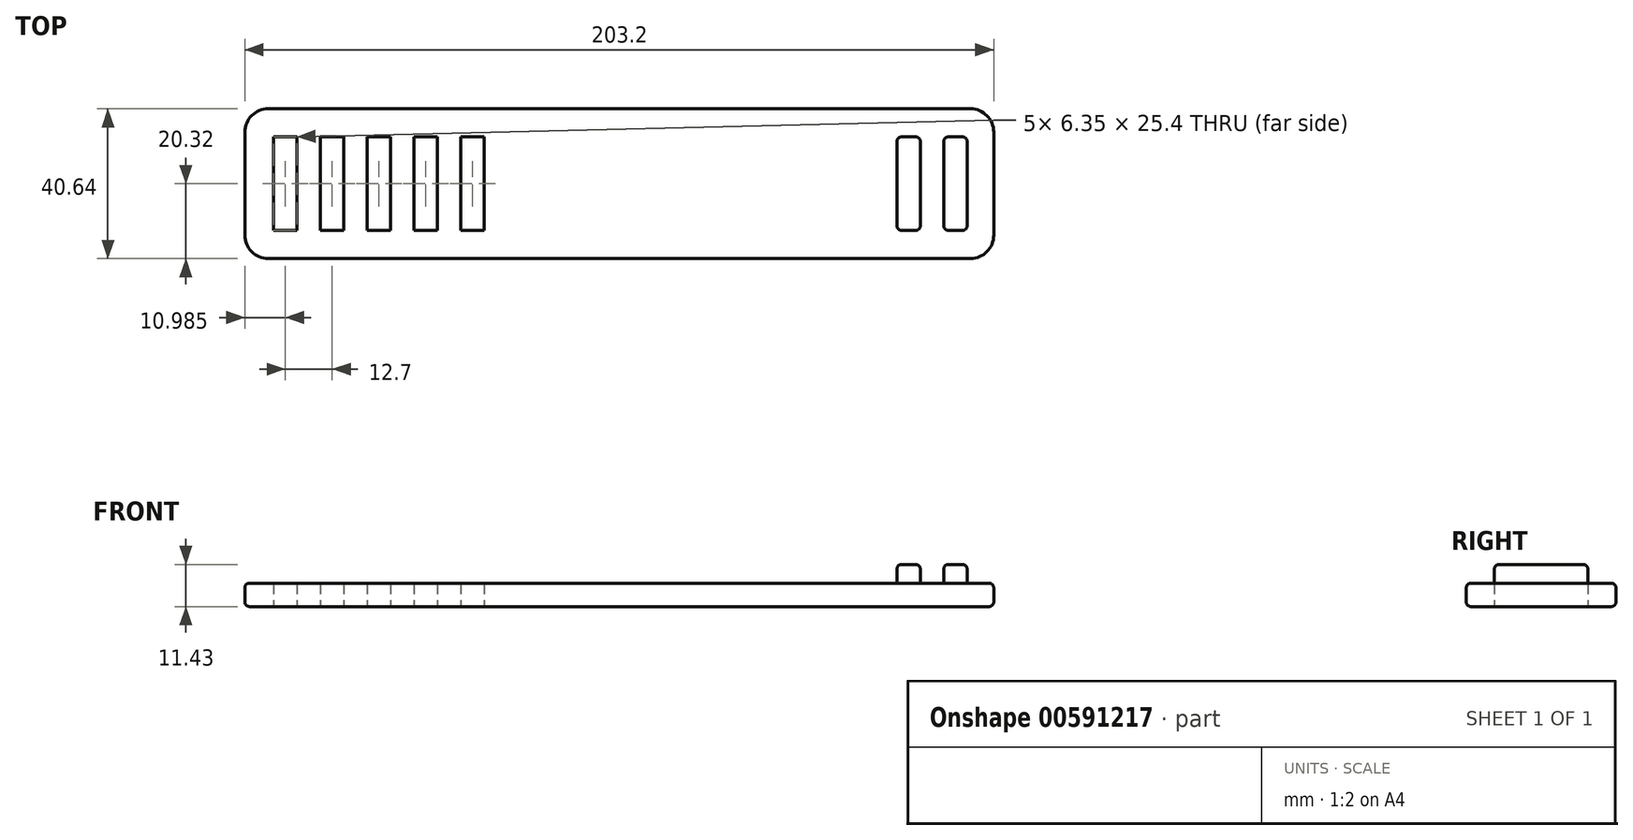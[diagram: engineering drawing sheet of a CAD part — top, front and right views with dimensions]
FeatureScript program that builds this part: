
annotation { "Feature Type Name" : "Feature", "Feature Type Description" : "" }
export const myFeature = defineFeature(function(context is Context, id is Id, definition is map)
    precondition{}
    {
        {
            var Q0;
            Q0=qCreatedBy(makeId("Top.planeOp"),FACE);
            var sketch = newSketch(context, id + "F0", { "sketchPlane" : qUnion([Q0])});
            skLineSegment(sketch, "E0.bottom", {"start": v(95.25, 20.32) * mm, "end": v(-95.25, 20.32) * mm});
            skLineSegment(sketch, "E0.top", {"start": v(95.25, -20.32) * mm, "end": v(-95.25, -20.32) * mm});
            skLineSegment(sketch, "E0.left", {"start": v(101.6, 13.97) * mm, "end": v(101.6, -13.97) * mm});
            skLineSegment(sketch, "E0.right", {"start": v(-101.6, 13.97) * mm, "end": v(-101.6, -13.97) * mm});
            skPoint(sketch, "E0.middle", {"position": v(0, 0) * mm});
            skCircle(sketch, "E1", {"center": v(4.14, 0) * mm, "radius": 17.56 * mm});
            skPoint(sketch, "E2.visualSharp", {"position": v(-101.6, 20.32) * mm});
            skArc(sketch, "E2.filletArc", {"start": v(-95.25, 20.32) * mm, "mid": v(-99.74, 18.46) * mm, "end": v(-101.6, 13.97) * mm});
            skPoint(sketch, "E3.visualSharp", {"position": v(-101.6, -20.32) * mm});
            skArc(sketch, "E3.filletArc", {"start": v(-101.6, -13.97) * mm, "mid": v(-99.74, -18.46) * mm, "end": v(-95.25, -20.32) * mm});
            skLineSegment(sketch, "E4.bottom", {"start": v(-87.44, 12.7) * mm, "end": v(-93.8, 12.7) * mm});
            skLineSegment(sketch, "E4.top", {"start": v(-87.44, -12.7) * mm, "end": v(-93.8, -12.7) * mm});
            skLineSegment(sketch, "E4.left", {"start": v(-87.44, 12.7) * mm, "end": v(-87.44, -12.7) * mm});
            skLineSegment(sketch, "E4.right", {"start": v(-93.8, 12.7) * mm, "end": v(-93.8, -12.7) * mm});
            skPoint(sketch, "E4.middle", {"position": v(-90.62, 0) * mm});
            skPoint(sketch, "E5.1.0.0", {"position": v(-77.92, 0) * mm});
            skLineSegment(sketch, "E5.1.0.1", {"start": v(-74.74, -12.7) * mm, "end": v(-81.1, -12.7) * mm});
            skLineSegment(sketch, "E5.1.0.2", {"start": v(-74.74, 12.7) * mm, "end": v(-74.74, -12.7) * mm});
            skLineSegment(sketch, "E5.1.0.3", {"start": v(-74.74, 12.7) * mm, "end": v(-81.1, 12.7) * mm});
            skLineSegment(sketch, "E5.1.0.4", {"start": v(-81.1, 12.7) * mm, "end": v(-81.1, -12.7) * mm});
            skPoint(sketch, "E5.2.0.0", {"position": v(-65.22, 0) * mm});
            skLineSegment(sketch, "E5.2.0.1", {"start": v(-62.04, -12.7) * mm, "end": v(-68.4, -12.7) * mm});
            skLineSegment(sketch, "E5.2.0.2", {"start": v(-62.04, 12.7) * mm, "end": v(-62.04, -12.7) * mm});
            skLineSegment(sketch, "E5.2.0.3", {"start": v(-62.04, 12.7) * mm, "end": v(-68.4, 12.7) * mm});
            skLineSegment(sketch, "E5.2.0.4", {"start": v(-68.4, 12.7) * mm, "end": v(-68.4, -12.7) * mm});
            skLineSegment(sketch, "E5.direction1", {"start": v(-93.8, -12.7) * mm, "end": v(-81.1, -12.7) * mm, "construction": true});
            skPoint(sketch, "E6.visualSharp", {"position": v(101.6, 20.32) * mm});
            skArc(sketch, "E6.filletArc", {"start": v(101.6, 13.97) * mm, "mid": v(99.74, 18.46) * mm, "end": v(95.25, 20.32) * mm});
            skPoint(sketch, "E7.visualSharp", {"position": v(101.6, -20.32) * mm});
            skArc(sketch, "E7.filletArc", {"start": v(95.25, -20.32) * mm, "mid": v(99.74, -18.46) * mm, "end": v(101.6, -13.97) * mm});
            skPoint(sketch, "E8.0.3.0", {"position": v(-52.52, 0) * mm});
            skLineSegment(sketch, "E8.1.3.0", {"start": v(-49.34, -12.7) * mm, "end": v(-55.7, -12.7) * mm});
            skLineSegment(sketch, "E8.4.3.0", {"start": v(-49.34, 12.7) * mm, "end": v(-49.34, -12.7) * mm});
            skLineSegment(sketch, "E8.7.3.0", {"start": v(-49.34, 12.7) * mm, "end": v(-55.7, 12.7) * mm});
            skLineSegment(sketch, "E8.10.3.0", {"start": v(-55.7, 12.7) * mm, "end": v(-55.7, -12.7) * mm});
            skPoint(sketch, "E8.0.4.0", {"position": v(-39.82, 0) * mm});
            skLineSegment(sketch, "E8.1.4.0", {"start": v(-36.64, -12.7) * mm, "end": v(-43, -12.7) * mm});
            skLineSegment(sketch, "E8.4.4.0", {"start": v(-36.64, 12.7) * mm, "end": v(-36.64, -12.7) * mm});
            skLineSegment(sketch, "E8.7.4.0", {"start": v(-36.64, 12.7) * mm, "end": v(-43, 12.7) * mm});
            skLineSegment(sketch, "E8.10.4.0", {"start": v(-43, 12.7) * mm, "end": v(-43, -12.7) * mm});
            skSolve(sketch);
        }
        {
            var Q0;
            Q0=makeQuery(id+"F0.imprint","IMPRINT",FACE,{"disambiguationData":[TD([[makeQuery(id+"F0.imprint","IMPRINT",EDGE,{"derivedFrom":sQuery(id+"F0.wireOp",EDGE,"E0.bottom")}),1.0]])]});
            var Q1;
            Q1=makeQuery(id+"F0.imprint","IMPRINT",FACE,{"disambiguationData":[TD([[makeQuery(id+"F0.imprint","IMPRINT",EDGE,{"derivedFrom":sQuery(id+"F0.wireOp",EDGE,"2bGg9E4l-DMj3-5FiE-Zovh-UfGB6S6LoPf9.top")}),-1.0]])]});
            var Q2;
            Q2=makeQuery(id+"F0.imprint","IMPRINT",FACE,{"disambiguationData":[TD([[makeQuery(id+"F0.imprint","IMPRINT",EDGE,{"derivedFrom":sQuery(id+"F0.wireOp",EDGE,"fidI8v6p-73p2-QQVa-uIKM-wmGhqBJP4heK.bottom")}),-1.0]])]});
            var Q3;
            Q3=makeQuery(id+"F0.imprint","IMPRINT",FACE,{"disambiguationData":[TD([[makeQuery(id+"F0.imprint","IMPRINT",EDGE,{"derivedFrom":sQuery(id+"F0.wireOp",EDGE,"E1")}),1.0]])]});
            extrude(context, id + "F1", {"entities" : qUnion([Q0, Q1, Q2, Q3]), "depth" : 6.35 * mm, "offsetDistance" : 25.4 * mm});
        }
        {
            var Q0;
            Q0=makeQuery(id+"F1.opExtrude","CAP_EDGE",EDGE,{"disambiguationData":[OSD([sQuery(id+"F0.wireOp",EDGE,"E0.top")])],"isStart":true});
            var Q1;
            Q1=makeQuery(id+"F1.opExtrude","CAP_EDGE",EDGE,{"disambiguationData":[OSD([sQuery(id+"F0.wireOp",EDGE,"E0.top")])],"isStart":false});
            fillet(context, id + "F2", {"entities" : qUnion([Q0, Q1]), "radius" : 1.27 * mm, "tangentPropagation" : true, "allowEdgeOverflow" : false});
        }
        {
            var Q0;
            Q0=makeQuery(id+"F1.opExtrude","CAP_FACE",FACE,{"disambiguationData":[OSD([sQuery(id+"F0.wireOp",EDGE,"E0.bottom"),sQuery(id+"F0.wireOp",EDGE,"E0.top"),sQuery(id+"F0.wireOp",EDGE,"E0.left"),sQuery(id+"F0.wireOp",EDGE,"E0.right"),sQuery(id+"F0.wireOp",EDGE,"E1"),sQuery(id+"F0.wireOp",EDGE,"E2.filletArc"),sQuery(id+"F0.wireOp",EDGE,"E3.filletArc"),sQuery(id+"F0.wireOp",EDGE,"E4.bottom"),sQuery(id+"F0.wireOp",EDGE,"E4.top"),sQuery(id+"F0.wireOp",EDGE,"E4.left"),sQuery(id+"F0.wireOp",EDGE,"E4.right"),sQuery(id+"F0.wireOp",EDGE,"E5.1.0.1"),sQuery(id+"F0.wireOp",EDGE,"E5.1.0.2"),sQuery(id+"F0.wireOp",EDGE,"E5.1.0.3"),sQuery(id+"F0.wireOp",EDGE,"E5.1.0.4"),sQuery(id+"F0.wireOp",EDGE,"E5.2.0.1"),sQuery(id+"F0.wireOp",EDGE,"E5.2.0.2"),sQuery(id+"F0.wireOp",EDGE,"E5.2.0.3"),sQuery(id+"F0.wireOp",EDGE,"E5.2.0.4"),sQuery(id+"F0.wireOp",EDGE,"E6.filletArc"),sQuery(id+"F0.wireOp",EDGE,"E7.filletArc"),sQuery(id+"F0.wireOp",EDGE,"E8.1.3.0"),sQuery(id+"F0.wireOp",EDGE,"E8.4.3.0"),sQuery(id+"F0.wireOp",EDGE,"E8.7.3.0"),sQuery(id+"F0.wireOp",EDGE,"E8.10.3.0"),sQuery(id+"F0.wireOp",EDGE,"E8.1.4.0"),sQuery(id+"F0.wireOp",EDGE,"E8.4.4.0"),sQuery(id+"F0.wireOp",EDGE,"E8.7.4.0"),sQuery(id+"F0.wireOp",EDGE,"E8.10.4.0")])],"isStart":false});
            var sketch = newSketch(context, id + "F3", { "sketchPlane" : qUnion([Q0])});
            skLineSegment(sketch, "E9.bottom", {"start": v(94.38, 12.7) * mm, "end": v(88.03, 12.7) * mm});
            skLineSegment(sketch, "E9.top", {"start": v(94.38, -12.7) * mm, "end": v(88.03, -12.7) * mm});
            skLineSegment(sketch, "E9.left", {"start": v(94.38, 12.7) * mm, "end": v(94.38, -12.7) * mm});
            skLineSegment(sketch, "E9.right", {"start": v(88.03, 12.7) * mm, "end": v(88.03, -12.7) * mm});
            skPoint(sketch, "E9.middle", {"position": v(91.2, 0) * mm});
            skLineSegment(sketch, "E10.1.0.0", {"start": v(75.33, 12.7) * mm, "end": v(75.33, -12.7) * mm});
            skLineSegment(sketch, "E10.1.0.1", {"start": v(81.68, -12.7) * mm, "end": v(75.33, -12.7) * mm});
            skLineSegment(sketch, "E10.1.0.2", {"start": v(81.68, 12.7) * mm, "end": v(81.68, -12.7) * mm});
            skLineSegment(sketch, "E10.1.0.3", {"start": v(81.68, 12.7) * mm, "end": v(75.33, 12.7) * mm});
            skPoint(sketch, "E10.1.0.4", {"position": v(78.5, 0) * mm});
            skLineSegment(sketch, "E10.direction1", {"start": v(88.03, -12.7) * mm, "end": v(75.33, -12.7) * mm, "construction": true});
            skCircle(sketch, "E11", {"center": v(0, 0) * mm, "radius": 18.22 * mm});
            skSolve(sketch);
        }
        {
            var Q0;
            Q0=makeQuery(id+"F3.imprint","IMPRINT",FACE,{"disambiguationData":[TD([[makeQuery(id+"F3.imprint","IMPRINT",EDGE,{"derivedFrom":sQuery(id+"F3.wireOp",EDGE,"E10.1.0.0")}),1.0]])]});
            var Q1;
            Q1=makeQuery(id+"F3.imprint","IMPRINT",FACE,{"disambiguationData":[TD([[makeQuery(id+"F3.imprint","IMPRINT",EDGE,{"derivedFrom":sQuery(id+"F3.wireOp",EDGE,"E9.bottom")}),1.0]])]});
            extrude(context, id + "F4", {"entities" : qUnion([Q0, Q1]), "operationType" : NewBodyOperationType.ADD, "depth" : 5.08 * mm, "offsetDistance" : 25.4 * mm});
        }
        {
            var Q0;
            Q0=makeQuery(id+"F4.opExtrude","CAP_EDGE",EDGE,{"disambiguationData":[OSD([sQuery(id+"F3.wireOp",EDGE,"E10.1.0.2")])],"isStart":false});
            var Q1;
            Q1=makeQuery(id+"F4.opExtrude","CAP_EDGE",EDGE,{"disambiguationData":[OSD([sQuery(id+"F3.wireOp",EDGE,"E10.1.0.1")])],"isStart":false});
            var Q2;
            Q2=makeQuery(id+"F4.opExtrude","CAP_EDGE",EDGE,{"disambiguationData":[OSD([sQuery(id+"F3.wireOp",EDGE,"E10.1.0.0")])],"isStart":false});
            var Q3;
            Q3=makeQuery(id+"F4.opExtrude","CAP_EDGE",EDGE,{"disambiguationData":[OSD([sQuery(id+"F3.wireOp",EDGE,"E10.1.0.3")])],"isStart":false});
            var Q4;
            Q4=makeQuery(id+"F4.opExtrude","CAP_EDGE",EDGE,{"disambiguationData":[OSD([sQuery(id+"F3.wireOp",EDGE,"E9.right")])],"isStart":false});
            var Q5;
            Q5=makeQuery(id+"F4.opExtrude","CAP_EDGE",EDGE,{"disambiguationData":[OSD([sQuery(id+"F3.wireOp",EDGE,"E9.left")])],"isStart":false});
            var Q6;
            Q6=makeQuery(id+"F4.opExtrude","CAP_EDGE",EDGE,{"disambiguationData":[OSD([sQuery(id+"F3.wireOp",EDGE,"E9.top")])],"isStart":false});
            var Q7;
            Q7=makeQuery(id+"F4.opExtrude","CAP_EDGE",EDGE,{"disambiguationData":[OSD([sQuery(id+"F3.wireOp",EDGE,"E9.bottom")])],"isStart":false});
            var Q8;
            Q8=makeQuery(id+"F4.opExtrude","SWEPT_EDGE",EDGE,{"disambiguationData":[OSD([sQuery(id+"F3.wireOp",EDGE,"E9.top"),sQuery(id+"F3.wireOp",EDGE,"E9.left")])]});
            var Q9;
            Q9=makeQuery(id+"F4.opExtrude","SWEPT_EDGE",EDGE,{"disambiguationData":[OSD([sQuery(id+"F3.wireOp",EDGE,"E9.top"),sQuery(id+"F3.wireOp",EDGE,"E9.right")])]});
            var Q10;
            Q10=makeQuery(id+"F4.opExtrude","SWEPT_EDGE",EDGE,{"disambiguationData":[OSD([sQuery(id+"F3.wireOp",EDGE,"E10.1.0.1"),sQuery(id+"F3.wireOp",EDGE,"E10.1.0.2")])]});
            var Q11;
            Q11=makeQuery(id+"F4.opExtrude","SWEPT_EDGE",EDGE,{"disambiguationData":[OSD([sQuery(id+"F3.wireOp",EDGE,"E10.1.0.0"),sQuery(id+"F3.wireOp",EDGE,"E10.1.0.1")])]});
            var Q12;
            Q12=makeQuery(id+"F4.opExtrude","SWEPT_EDGE",EDGE,{"disambiguationData":[OSD([sQuery(id+"F3.wireOp",EDGE,"E10.1.0.2"),sQuery(id+"F3.wireOp",EDGE,"E10.1.0.3")])]});
            var Q13;
            Q13=makeQuery(id+"F4.opExtrude","SWEPT_EDGE",EDGE,{"disambiguationData":[OSD([sQuery(id+"F3.wireOp",EDGE,"E9.bottom"),sQuery(id+"F3.wireOp",EDGE,"E9.left")])]});
            var Q14;
            Q14=makeQuery(id+"F4.opExtrude","SWEPT_EDGE",EDGE,{"disambiguationData":[OSD([sQuery(id+"F3.wireOp",EDGE,"E9.bottom"),sQuery(id+"F3.wireOp",EDGE,"E9.right")])]});
            var Q15;
            Q15=makeQuery(id+"F4.opExtrude","SWEPT_EDGE",EDGE,{"disambiguationData":[OSD([sQuery(id+"F3.wireOp",EDGE,"E10.1.0.0"),sQuery(id+"F3.wireOp",EDGE,"E10.1.0.3")])]});
            fillet(context, id + "F5", {"entities" : qUnion([Q0, Q1, Q2, Q3, Q4, Q5, Q6, Q7, Q8, Q9, Q10, Q11, Q12, Q13, Q14, Q15]), "radius" : 1.27 * mm, "tangentPropagation" : true, "allowEdgeOverflow" : false});
        }
    });
